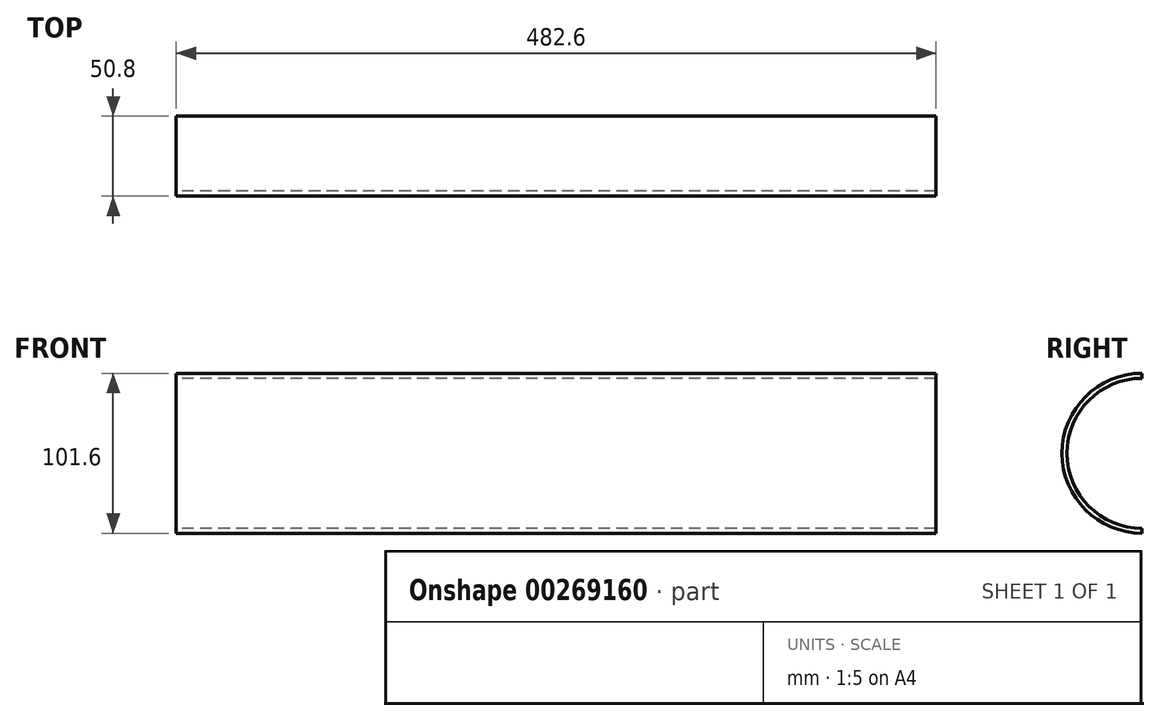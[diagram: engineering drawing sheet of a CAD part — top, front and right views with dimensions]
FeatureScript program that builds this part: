
annotation { "Feature Type Name" : "Feature", "Feature Type Description" : "" }
export const myFeature = defineFeature(function(context is Context, id is Id, definition is map)
    precondition{}
    {
        {
            var Q0;
            Q0=qCreatedBy(makeId("Right.planeOp"),FACE);
            var sketch = newSketch(context, id + "F0", { "sketchPlane" : qUnion([Q0])});
            skCircle(sketch, "E0", {"center": v(0, 0) * mm, "radius": 50.8 * mm});
            skCircle(sketch, "E1", {"center": v(0, 0) * mm, "radius": 47.63 * mm});
            skSolve(sketch);
        }
        {
            var Q0;
            Q0=makeQuery(id+"F0.imprint","IMPRINT",FACE,{"disambiguationData":[TD([[makeQuery(id+"F0.imprint","IMPRINT",EDGE,{"derivedFrom":sQuery(id+"F0.wireOp",EDGE,"E0")}),1.0]])]});
            extrude(context, id + "F1", {"entities" : qUnion([Q0]), "depth" : 482.6 * mm});
        }
        {
            var Q0;
            Q0=qCreatedBy(makeId("Top.planeOp"),FACE);
            var sketch = newSketch(context, id + "F2", { "sketchPlane" : qUnion([Q0])});
            skArc(sketch, "E2", {"start": v(48.9, 0) * mm, "mid": v(74.3, -25.4) * mm, "end": v(99.7, 0) * mm});
            skArc(sketch, "E3.0", {"start": v(43.2, 6.35) * mm, "mid": v(74.3, -31.75) * mm, "end": v(105.41, 6.35) * mm});
            skSolve(sketch);
        }
        {
            var Q0;
            Q0=qCreatedBy(makeId("Right.planeOp"),FACE);
            var sketch = newSketch(context, id + "F3", { "sketchPlane" : qUnion([Q0])});
            skLineSegment(sketch, "E4", {"start": v(0, 0) * mm, "end": v(0, -77.1) * mm});
            skLineSegment(sketch, "E5", {"start": v(0, 0) * mm, "end": v(0, 91.05) * mm});
            skLineSegment(sketch, "E6", {"start": v(0, 91.05) * mm, "end": v(62, 91.05) * mm});
            skLineSegment(sketch, "E7", {"start": v(62, 91.05) * mm, "end": v(62, -77.1) * mm});
            skLineSegment(sketch, "E8", {"start": v(62, -77.1) * mm, "end": v(0, -77.1) * mm});
            skSolve(sketch);
        }
        {
            var Q0;
            Q0=makeQuery(id+"F3.imprint","IMPRINT",FACE,{"disambiguationData":[TD([[makeQuery(id+"F3.imprint","IMPRINT",EDGE,{"derivedFrom":sQuery(id+"F3.wireOp",EDGE,"E4")}),1.0]])]});
            extrude(context, id + "F4", {"entities" : qUnion([Q0]), "operationType" : NewBodyOperationType.REMOVE, "depth" : 508 * mm});
        }
        {
            var Q0;
            Q0=qCreatedBy(makeId("Right.planeOp"),FACE);
            var sketch = newSketch(context, id + "F5", { "sketchPlane" : qUnion([Q0])});
            skLineSegment(sketch, "E9", {"start": v(0, 0) * mm, "end": v(0, 92.08) * mm});
            skLineSegment(sketch, "E10", {"start": v(0, 92.08) * mm, "end": v(55.55, 92.08) * mm});
            skLineSegment(sketch, "E11", {"start": v(55.55, 92.08) * mm, "end": v(55.55, 0) * mm});
            skLineSegment(sketch, "E12", {"start": v(55.55, 0) * mm, "end": v(0, 0) * mm});
            skSolve(sketch);
        }
        {
            var Q0;
            Q0=makeQuery(id+"F5.imprint","IMPRINT",FACE,{"disambiguationData":[TD([[makeQuery(id+"F5.imprint","IMPRINT",EDGE,{"derivedFrom":sQuery(id+"F5.wireOp",EDGE,"E9")}),-1.0]])]});
            extrude(context, id + "F6", {"entities" : qUnion([Q0]), "operationType" : NewBodyOperationType.REMOVE, "depth" : 508 * mm});
        }
        {
            var Q0;
            Q0=qCreatedBy(makeId("Top.planeOp"),FACE);
            var sketch = newSketch(context, id + "F7", { "sketchPlane" : qUnion([Q0])});
            skLineSegment(sketch, "E13", {"start": v(0, 0) * mm, "end": v(106.59, 0) * mm});
            skLineSegment(sketch, "E14", {"start": v(106.59, 0) * mm, "end": v(106.59, 48.04) * mm});
            skLineSegment(sketch, "E15", {"start": v(106.59, 48.04) * mm, "end": v(0, 48.04) * mm});
            skLineSegment(sketch, "E16", {"start": v(0, 48.04) * mm, "end": v(0, 0) * mm});
            skSolve(sketch);
        }
        {
            var Q0;
            Q0=makeQuery(id+"F7.imprint","IMPRINT",FACE,{"disambiguationData":[TD([[makeQuery(id+"F7.imprint","IMPRINT",EDGE,{"derivedFrom":sQuery(id+"F7.wireOp",EDGE,"E13")}),1.0]])]});
            extrude(context, id + "F8", {"entities" : qUnion([Q0]), "operationType" : NewBodyOperationType.REMOVE, "depth" : 101.6 * mm});
        }
        {
            var Q0;
            Q0=qCreatedBy(makeId("Top.planeOp"),FACE);
            var sketch = newSketch(context, id + "F9", { "sketchPlane" : qUnion([Q0])});
            skLineSegment(sketch, "E17.bottom", {"start": v(48.33, 0) * mm, "end": v(106.8, 0) * mm});
            skLineSegment(sketch, "E17.top", {"start": v(48.33, 32.7) * mm, "end": v(106.8, 32.7) * mm});
            skLineSegment(sketch, "E17.left", {"start": v(48.33, 0) * mm, "end": v(48.33, 32.7) * mm});
            skLineSegment(sketch, "E17.right", {"start": v(106.8, 0) * mm, "end": v(106.8, 32.7) * mm});
            skSolve(sketch);
        }
        {
            var Q0;
            Q0=makeQuery(id+"F9.imprint","IMPRINT",FACE,{"disambiguationData":[TD([[makeQuery(id+"F9.imprint","IMPRINT",EDGE,{"derivedFrom":sQuery(id+"F9.wireOp",EDGE,"E17.bottom")}),1.0]])]});
            extrude(context, id + "F10", {"entities" : qUnion([Q0]), "operationType" : NewBodyOperationType.REMOVE, "depth" : 82.55 * mm});
        }
        {
            var Q0;
            Q0=sQuery(id+"F2.wireOp",EDGE,"E2");
            var Q1;
            Q1=sQuery(id+"F2.wireOp",EDGE,"E3.0");
            extrude(context, id + "F11", {"bodyType" : ToolBodyType.SURFACE, "surfaceEntities" : qUnion([Q0, Q1]), "oppositeDirection" : true, "depth" : 82.55 * mm});
        }
    });
